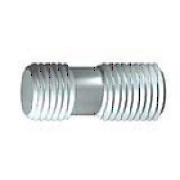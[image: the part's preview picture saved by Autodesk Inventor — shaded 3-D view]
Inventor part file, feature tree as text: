
AUTODESK INVENTOR PART (.ipt)
format: ipt  version: 2023 (Build 270158000, 158)  size: 164,352 bytes
history: native  units: mm
features: sketch x2, plane x1, other x1
ambient origin geometry x8: Origin, YZ Plane, XZ Plane, XY Plane, X Axis, Y Axis, Z Axis, Center Point
bodies: Solid1 (feature_tree)
feature tree (4):
  plane  "Work Plane1"
  sketch  "Sketch1"  dims[d1=12.0mm]
  sketch  "Sketch2"  dims[d3=10.829mm d4=24.0mm d5=48.0mm d6=30.0mm d7=90.0deg d8=24.0mm d9=0.0mm d2=10.829mm d29=30.0mm d30=0.0mm d31=0.8mm d32=2.0mm d33=45.0deg d34=-24.0mm d35=12.0mm d37=0.4mm d38=2.0mm d39=45.0deg d40=0.0mm d42=0.0mm]
  other  "Srf1"
